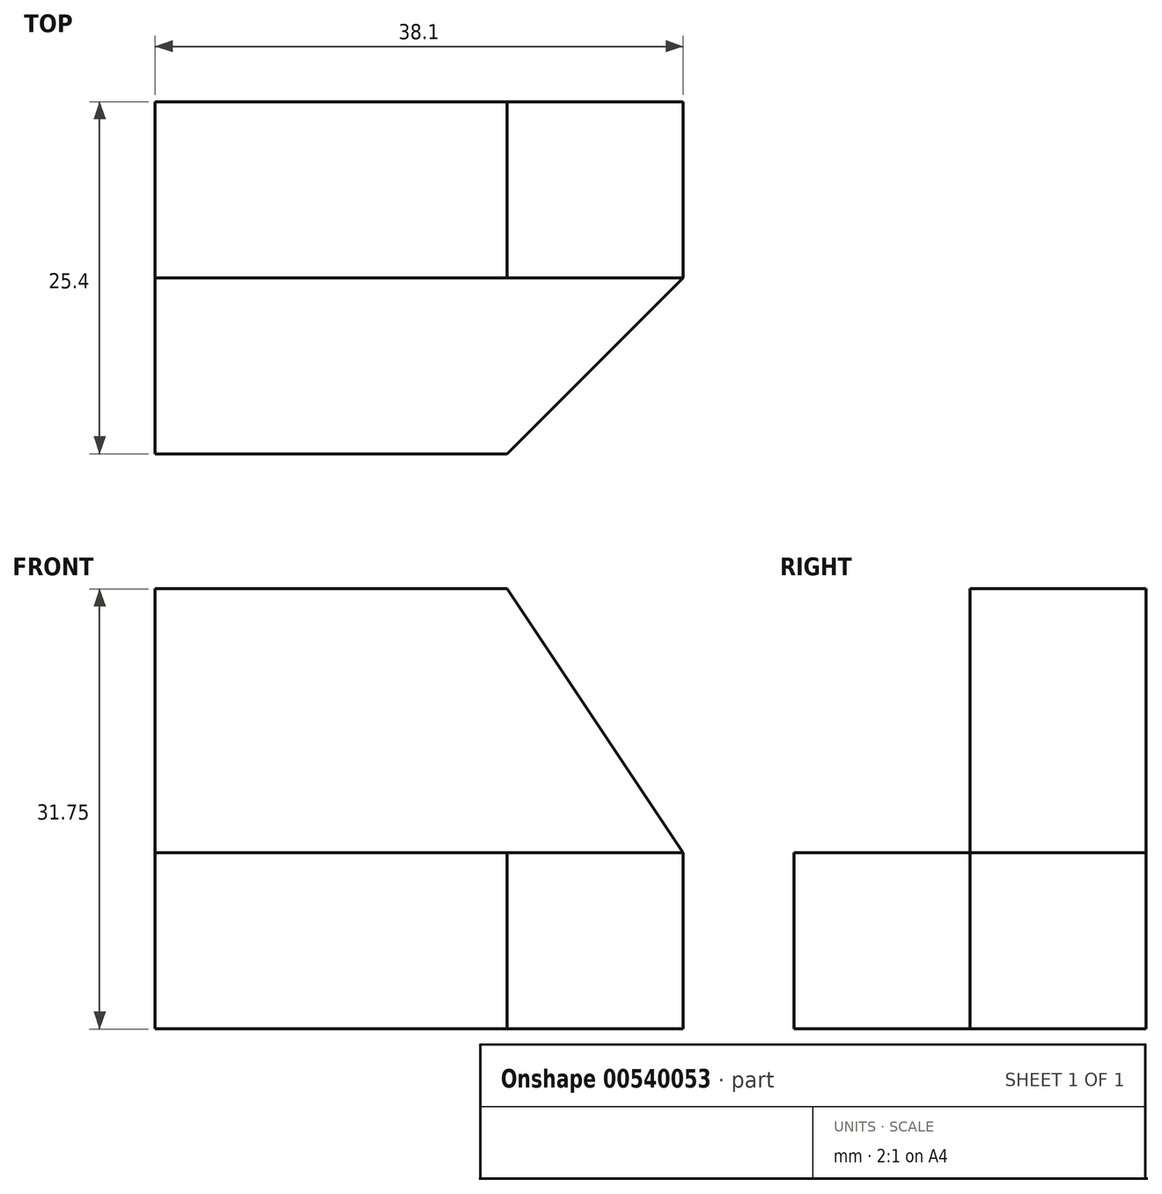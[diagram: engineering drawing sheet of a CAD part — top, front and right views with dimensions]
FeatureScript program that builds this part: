
annotation { "Feature Type Name" : "Feature", "Feature Type Description" : "" }
export const myFeature = defineFeature(function(context is Context, id is Id, definition is map)
    precondition{}
    {
        {
            var Q0;
            Q0=qCreatedBy(makeId("Front.planeOp"),FACE);
            var sketch = newSketch(context, id + "F0", { "sketchPlane" : qUnion([Q0])});
            skLineSegment(sketch, "E0", {"start": v(-61.32, 57.63) * mm, "end": v(-61.32, 25.88) * mm});
            skLineSegment(sketch, "E1", {"start": v(-61.32, 25.88) * mm, "end": v(-23.22, 25.88) * mm});
            skLineSegment(sketch, "E2", {"start": v(-23.22, 25.88) * mm, "end": v(-23.22, 57.63) * mm});
            skLineSegment(sketch, "E3", {"start": v(-23.22, 57.63) * mm, "end": v(-61.32, 57.63) * mm});
            skSolve(sketch);
        }
        {
            var Q0;
            Q0=makeQuery(id+"F0.imprint","IMPRINT",FACE,{"disambiguationData":[TD([[makeQuery(id+"F0.imprint","IMPRINT",EDGE,{"derivedFrom":sQuery(id+"F0.wireOp",EDGE,"E0")}),1.0]])]});
            extrude(context, id + "F1", {"entities" : qUnion([Q0]), "depth" : 25.4 * mm, "offsetDistance" : 25.4 * mm});
        }
        {
            var Q0;
            Q0=makeQuery(id+"F1.opExtrude","SWEPT_FACE",FACE,{"disambiguationData":[OSD([sQuery(id+"F0.wireOp",EDGE,"E0")])]});
            var sketch = newSketch(context, id + "F2", { "sketchPlane" : qUnion([Q0])});
            skLineSegment(sketch, "E4", {"start": v(12.7, 57.63) * mm, "end": v(12.7, 38.58) * mm});
            skLineSegment(sketch, "E5", {"start": v(12.7, 38.58) * mm, "end": v(25.4, 38.58) * mm});
            skSolve(sketch);
        }
        {
            var Q0;
            {var subQ0=sQuery(id+"F2.wireOp",EDGE,"E4");Q0=makeQuery(id+"F2.imprint","IMPRINT",FACE,{"disambiguationData":[TD([[makeQuery(id+"F2.imprint","IMPRINT",EDGE,{"derivedFrom":subQ0}),1.0]])]});}
            extrude(context, id + "F3", {"entities" : qUnion([Q0]), "operationType" : NewBodyOperationType.REMOVE, "oppositeDirection" : true, "depth" : 38.1 * mm, "offsetDistance" : 25.4 * mm});
        }
        {
            var Q0;
            Q0=makeQuery(id+"F3.boolean.opBoolean","COPY",FACE,{"derivedFrom":makeQuery(id+"F3.opExtrude","SWEPT_FACE",FACE,{"disambiguationData":[OSD([sQuery(id+"F2.wireOp",EDGE,"E4")])]})});
            var sketch = newSketch(context, id + "F4", { "sketchPlane" : qUnion([Q0])});
            skLineSegment(sketch, "E6", {"start": v(-35.92, 57.63) * mm, "end": v(-23.22, 38.58) * mm});
            skLineSegment(sketch, "E7", {"start": v(-23.22, 38.58) * mm, "end": v(-10.52, 38.58) * mm});
            skSolve(sketch);
        }
        {
            var Q0;
            {var subQ0=sQuery(id+"F4.wireOp",EDGE,"E6");Q0=makeQuery(id+"F4.imprint","IMPRINT",FACE,{"disambiguationData":[TD([[makeQuery(id+"F4.imprint","IMPRINT",EDGE,{"derivedFrom":subQ0}),1.0]])]});}
            extrude(context, id + "F5", {"entities" : qUnion([Q0]), "operationType" : NewBodyOperationType.REMOVE, "oppositeDirection" : true, "depth" : 25.4 * mm, "offsetDistance" : 25.4 * mm});
        }
        {
            var Q0;
            Q0=makeQuery(id+"F3.boolean.opBoolean","COPY",FACE,{"derivedFrom":makeQuery(id+"F3.opExtrude","SWEPT_FACE",FACE,{"disambiguationData":[OSD([sQuery(id+"F2.wireOp",EDGE,"E5")])]})});
            var sketch = newSketch(context, id + "F6", { "sketchPlane" : qUnion([Q0])});
            skLineSegment(sketch, "E8", {"start": v(-23.22, -12.7) * mm, "end": v(-35.92, -25.4) * mm});
            skSolve(sketch);
        }
        {
            var Q0;
            {var subQ0=sQuery(id+"F6.wireOp",EDGE,"E8");Q0=makeQuery(id+"F6.imprint","IMPRINT",FACE,{"disambiguationData":[TD([[makeQuery(id+"F6.imprint","IMPRINT",EDGE,{"derivedFrom":subQ0}),1.0]])]});}
            extrude(context, id + "F7", {"entities" : qUnion([Q0]), "operationType" : NewBodyOperationType.REMOVE, "oppositeDirection" : true, "depth" : 25.4 * mm, "offsetDistance" : 25.4 * mm});
        }
    });
